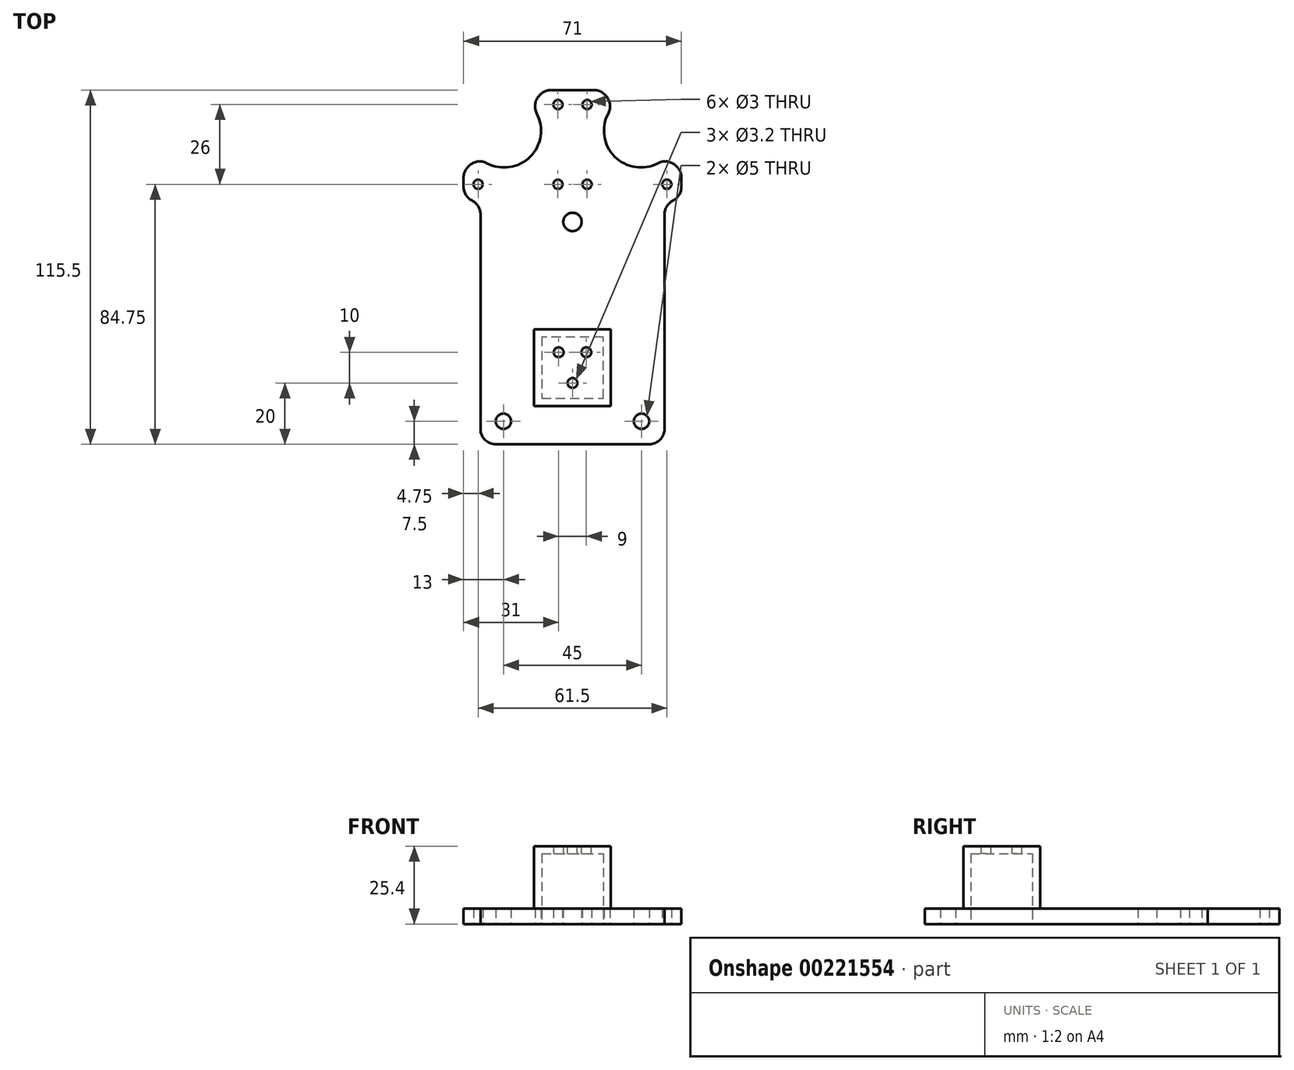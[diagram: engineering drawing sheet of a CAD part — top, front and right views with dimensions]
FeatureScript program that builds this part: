
annotation { "Feature Type Name" : "Feature", "Feature Type Description" : "" }
export const myFeature = defineFeature(function(context is Context, id is Id, definition is map)
    precondition{}
    {
        {
            var Q0;
            Q0=qCreatedBy(makeId("Top.planeOp"),FACE);
            var sketch = newSketch(context, id + "F0", { "sketchPlane" : qUnion([Q0])});
            skLineSegment(sketch, "E0.bottom", {"start": v(0, 0) * mm, "end": v(60, 0) * mm});
            skLineSegment(sketch, "E0.left", {"start": v(0, 0) * mm, "end": v(0, 80) * mm});
            skLineSegment(sketch, "E0.right", {"start": v(60, 0) * mm, "end": v(60, 80) * mm});
            skCircle(sketch, "E1", {"center": v(30, 72.5) * mm, "radius": 3 * mm});
            skCircle(sketch, "E2", {"center": v(52.5, 7.5) * mm, "radius": 2.5 * mm});
            skCircle(sketch, "E3", {"center": v(7.5, 7.5) * mm, "radius": 2.5 * mm});
            skLineSegment(sketch, "E4", {"start": v(0, 80) * mm, "end": v(-5.5, 80) * mm});
            skLineSegment(sketch, "E5", {"start": v(60, 80) * mm, "end": v(65.5, 80) * mm});
            skLineSegment(sketch, "E6.top", {"start": v(30, 80) * mm, "end": v(-5.5, 80) * mm, "construction": true});
            skLineSegment(sketch, "E6.left", {"start": v(30, 115.5) * mm, "end": v(30, 80) * mm, "construction": true});
            skCircle(sketch, "E7", {"center": v(25.25, 110.75) * mm, "radius": 1.5 * mm});
            skCircle(sketch, "E8", {"center": v(25.25, 84.75) * mm, "radius": 1.5 * mm});
            skCircle(sketch, "E9", {"center": v(-0.75, 84.75) * mm, "radius": 1.5 * mm});
            skCircle(sketch, "E10.MirrorC", {"center": v(60.75, 84.75) * mm, "radius": 1.5 * mm});
            skCircle(sketch, "E11.MirrorC", {"center": v(34.75, 84.75) * mm, "radius": 1.5 * mm});
            skCircle(sketch, "E12.MirrorC", {"center": v(34.75, 110.75) * mm, "radius": 1.5 * mm});
            skLineSegment(sketch, "E13", {"start": v(-5.5, 80) * mm, "end": v(-5.5, 89) * mm});
            skLineSegment(sketch, "E14", {"start": v(21, 115.5) * mm, "end": v(39, 115.5) * mm});
            skArc(sketch, "E15", {"start": v(-0.74, 93.76) * mm, "mid": v(16.24, 93.76) * mm, "end": v(16.24, 110.74) * mm});
            skLineSegment(sketch, "E16", {"start": v(-5.5, 89) * mm, "end": v(-0.74, 93.76) * mm});
            skLineSegment(sketch, "E17", {"start": v(16.24, 110.74) * mm, "end": v(21, 115.5) * mm});
            skLineSegment(sketch, "E18.MirrorCS", {"start": v(65.5, 80) * mm, "end": v(65.5, 89) * mm});
            skLineSegment(sketch, "E19.MirrorCS", {"start": v(43.76, 110.74) * mm, "end": v(39, 115.5) * mm});
            skLineSegment(sketch, "E20.MirrorCS", {"start": v(65.5, 89) * mm, "end": v(60.74, 93.76) * mm});
            skArc(sketch, "E21.MirrorCS", {"start": v(60.74, 93.76) * mm, "mid": v(43.76, 93.76) * mm, "end": v(43.76, 110.74) * mm});
            skSolve(sketch);
        }
        {
            var Q0;
            Q0 = qSketchRegion(id + "F0", true);
            extrude(context, id + "F1", {"entities" : qUnion([Q0]), "depth" : 5 * mm});
        }
        {
            var Q0;
            Q0=makeQuery(id+"F1.opExtrude","SWEPT_EDGE",EDGE,{"disambiguationData":[OSD([sQuery(id+"F0.wireOp",EDGE,"E0.top"),sQuery(id+"F0.wireOp",EDGE,"E0.left")])]});
            var Q1;
            Q1=makeQuery(id+"F1.opExtrude","SWEPT_EDGE",EDGE,{"disambiguationData":[OSD([sQuery(id+"F0.wireOp",EDGE,"E0.top"),sQuery(id+"F0.wireOp",EDGE,"E0.right")])]});
            var Q2;
            Q2=makeQuery(id+"F1.opExtrude","SWEPT_EDGE",EDGE,{"disambiguationData":[OSD([sQuery(id+"F0.wireOp",EDGE,"E0.bottom"),sQuery(id+"F0.wireOp",EDGE,"E0.right")])]});
            var Q3;
            Q3=makeQuery(id+"F1.opExtrude","SWEPT_EDGE",EDGE,{"disambiguationData":[OSD([sQuery(id+"F0.wireOp",EDGE,"E0.bottom"),sQuery(id+"F0.wireOp",EDGE,"E0.left")])]});
            fillet(context, id + "F2", {"entities" : qUnion([Q0, Q1, Q2, Q3]), "radius" : 5 * mm, "tangentPropagation" : true, "allowEdgeOverflow" : false});
        }
        {
            var Q0;
            Q0=makeQuery(id+"F1.opExtrude","SWEPT_EDGE",EDGE,{"disambiguationData":[OSD([sQuery(id+"F0.wireOp",EDGE,"E4"),sQuery(id+"F0.wireOp",EDGE,"E13")])]});
            var Q1;
            Q1=makeQuery(id+"F1.opExtrude","SWEPT_EDGE",EDGE,{"disambiguationData":[OSD([sQuery(id+"F0.wireOp",EDGE,"E13"),sQuery(id+"F0.wireOp",EDGE,"E16")])]});
            var Q2;
            Q2=makeQuery(id+"F1.opExtrude","SWEPT_EDGE",EDGE,{"disambiguationData":[OSD([sQuery(id+"F0.wireOp",EDGE,"E15"),sQuery(id+"F0.wireOp",EDGE,"E16")])]});
            var Q3;
            Q3=makeQuery(id+"F1.opExtrude","SWEPT_EDGE",EDGE,{"disambiguationData":[OSD([sQuery(id+"F0.wireOp",EDGE,"E15"),sQuery(id+"F0.wireOp",EDGE,"E17")])]});
            var Q4;
            Q4=makeQuery(id+"F1.opExtrude","SWEPT_EDGE",EDGE,{"disambiguationData":[OSD([sQuery(id+"F0.wireOp",EDGE,"E14"),sQuery(id+"F0.wireOp",EDGE,"E17")])]});
            var Q5;
            Q5=makeQuery(id+"F1.opExtrude","SWEPT_EDGE",EDGE,{"disambiguationData":[OSD([sQuery(id+"F0.wireOp",EDGE,"E5"),sQuery(id+"F0.wireOp",EDGE,"E18.MirrorCS")])]});
            var Q6;
            Q6=makeQuery(id+"F1.opExtrude","SWEPT_EDGE",EDGE,{"disambiguationData":[OSD([sQuery(id+"F0.wireOp",EDGE,"E18.MirrorCS"),sQuery(id+"F0.wireOp",EDGE,"E20.MirrorCS")])]});
            var Q7;
            Q7=makeQuery(id+"F1.opExtrude","SWEPT_EDGE",EDGE,{"disambiguationData":[OSD([sQuery(id+"F0.wireOp",EDGE,"E20.MirrorCS"),sQuery(id+"F0.wireOp",EDGE,"E21.MirrorCS")])]});
            var Q8;
            Q8=makeQuery(id+"F1.opExtrude","SWEPT_EDGE",EDGE,{"disambiguationData":[OSD([sQuery(id+"F0.wireOp",EDGE,"E19.MirrorCS"),sQuery(id+"F0.wireOp",EDGE,"E21.MirrorCS")])]});
            var Q9;
            Q9=makeQuery(id+"F1.opExtrude","SWEPT_EDGE",EDGE,{"disambiguationData":[OSD([sQuery(id+"F0.wireOp",EDGE,"E14"),sQuery(id+"F0.wireOp",EDGE,"E19.MirrorCS")])]});
            fillet(context, id + "F3", {"entities" : qUnion([Q0, Q1, Q2, Q3, Q4, Q5, Q6, Q7, Q8, Q9]), "radius" : 5 * mm, "tangentPropagation" : true, "allowEdgeOverflow" : false});
        }
        {
            var Q0;
            Q0=makeQuery(id+"F1.opExtrude","CAP_FACE",FACE,{"disambiguationData":[OSD([sQuery(id+"F0.wireOp",EDGE,"E0.bottom"),sQuery(id+"F0.wireOp",EDGE,"E0.left"),sQuery(id+"F0.wireOp",EDGE,"E0.right"),sQuery(id+"F0.wireOp",EDGE,"E1"),sQuery(id+"F0.wireOp",EDGE,"E2"),sQuery(id+"F0.wireOp",EDGE,"E3"),sQuery(id+"F0.wireOp",EDGE,"E4"),sQuery(id+"F0.wireOp",EDGE,"E5"),sQuery(id+"F0.wireOp",EDGE,"E7"),sQuery(id+"F0.wireOp",EDGE,"E8"),sQuery(id+"F0.wireOp",EDGE,"E9"),sQuery(id+"F0.wireOp",EDGE,"E10.MirrorC"),sQuery(id+"F0.wireOp",EDGE,"E11.MirrorC"),sQuery(id+"F0.wireOp",EDGE,"E12.MirrorC"),sQuery(id+"F0.wireOp",EDGE,"E13"),sQuery(id+"F0.wireOp",EDGE,"E14"),sQuery(id+"F0.wireOp",EDGE,"E15"),sQuery(id+"F0.wireOp",EDGE,"E16"),sQuery(id+"F0.wireOp",EDGE,"E17"),sQuery(id+"F0.wireOp",EDGE,"E18.MirrorCS"),sQuery(id+"F0.wireOp",EDGE,"E19.MirrorCS"),sQuery(id+"F0.wireOp",EDGE,"E20.MirrorCS"),sQuery(id+"F0.wireOp",EDGE,"E21.MirrorCS")])],"isStart":false});
            var sketch = newSketch(context, id + "F4", { "sketchPlane" : qUnion([Q0])});
            skLineSegment(sketch, "E22.bottom", {"start": v(15, 0) * mm, "end": v(45, 0) * mm, "construction": true});
            skLineSegment(sketch, "E23", {"start": v(30, 40) * mm, "end": v(30, 10) * mm, "construction": true});
            skLineSegment(sketch, "E24.bottom", {"start": v(17.5, 37.5) * mm, "end": v(42.5, 37.5) * mm});
            skLineSegment(sketch, "E24.top", {"start": v(17.5, 12.5) * mm, "end": v(42.5, 12.5) * mm});
            skLineSegment(sketch, "E24.left", {"start": v(17.5, 37.5) * mm, "end": v(17.5, 12.5) * mm});
            skLineSegment(sketch, "E24.right", {"start": v(42.5, 37.5) * mm, "end": v(42.5, 12.5) * mm});
            skSolve(sketch);
        }
        {
            var Q0;
            Q0 = qSketchRegion(id + "F4", true);
            extrude(context, id + "F5", {"entities" : qUnion([Q0]), "operationType" : NewBodyOperationType.ADD, "depth" : 20.4 * mm});
        }
        {
            var Q0;
            Q0=makeQuery(id+"F1.opExtrude","CAP_FACE",FACE,{"disambiguationData":[OSD([sQuery(id+"F0.wireOp",EDGE,"E0.bottom"),sQuery(id+"F0.wireOp",EDGE,"E0.left"),sQuery(id+"F0.wireOp",EDGE,"E0.right"),sQuery(id+"F0.wireOp",EDGE,"E1"),sQuery(id+"F0.wireOp",EDGE,"E2"),sQuery(id+"F0.wireOp",EDGE,"E3"),sQuery(id+"F0.wireOp",EDGE,"E4"),sQuery(id+"F0.wireOp",EDGE,"E5"),sQuery(id+"F0.wireOp",EDGE,"E7"),sQuery(id+"F0.wireOp",EDGE,"E8"),sQuery(id+"F0.wireOp",EDGE,"E9"),sQuery(id+"F0.wireOp",EDGE,"E10.MirrorC"),sQuery(id+"F0.wireOp",EDGE,"E11.MirrorC"),sQuery(id+"F0.wireOp",EDGE,"E12.MirrorC"),sQuery(id+"F0.wireOp",EDGE,"E13"),sQuery(id+"F0.wireOp",EDGE,"E14"),sQuery(id+"F0.wireOp",EDGE,"E15"),sQuery(id+"F0.wireOp",EDGE,"E16"),sQuery(id+"F0.wireOp",EDGE,"E17"),sQuery(id+"F0.wireOp",EDGE,"E18.MirrorCS"),sQuery(id+"F0.wireOp",EDGE,"E19.MirrorCS"),sQuery(id+"F0.wireOp",EDGE,"E20.MirrorCS"),sQuery(id+"F0.wireOp",EDGE,"E21.MirrorCS")])],"isStart":true});
            var sketch = newSketch(context, id + "F6", { "sketchPlane" : qUnion([Q0])});
            skLineSegment(sketch, "E25.0.0", {"start": v(17.5, -37.5) * mm, "end": v(17.5, -12.5) * mm, "construction": true});
            skLineSegment(sketch, "E25.0.1", {"start": v(17.5, -12.5) * mm, "end": v(42.5, -12.5) * mm, "construction": true});
            skLineSegment(sketch, "E25.0.2", {"start": v(42.5, -12.5) * mm, "end": v(42.5, -37.5) * mm, "construction": true});
            skLineSegment(sketch, "E25.0.3", {"start": v(42.5, -37.5) * mm, "end": v(17.5, -37.5) * mm, "construction": true});
            skLineSegment(sketch, "E26.0", {"start": v(40, -15) * mm, "end": v(40, -35) * mm});
            skLineSegment(sketch, "E26.1", {"start": v(20, -15) * mm, "end": v(40, -15) * mm});
            skLineSegment(sketch, "E26.2", {"start": v(20, -35) * mm, "end": v(20, -15) * mm});
            skLineSegment(sketch, "E26.3", {"start": v(40, -35) * mm, "end": v(20, -35) * mm});
            skSolve(sketch);
        }
        {
            var Q0;
            Q0 = qSketchRegion(id + "F6", true);
            extrude(context, id + "F7", {"entities" : qUnion([Q0]), "operationType" : NewBodyOperationType.REMOVE, "oppositeDirection" : true, "depth" : (25.4 - 2.5) * mm});
        }
        {
            var Q0;
            Q0=makeQuery(id+"F5.opExtrude","CAP_FACE",FACE,{"disambiguationData":[OSD([sQuery(id+"F4.wireOp",EDGE,"E24.bottom"),sQuery(id+"F4.wireOp",EDGE,"E24.top"),sQuery(id+"F4.wireOp",EDGE,"E24.left"),sQuery(id+"F4.wireOp",EDGE,"E24.right")])],"isStart":false});
            var sketch = newSketch(context, id + "F8", { "sketchPlane" : qUnion([Q0])});
            skLineSegment(sketch, "E27", {"start": v(30, 37.5) * mm, "end": v(30, 12.5) * mm, "construction": true});
            skCircle(sketch, "E28", {"center": v(25.5, 30) * mm, "radius": 1.6 * mm});
            skCircle(sketch, "E29", {"center": v(30, 20) * mm, "radius": 1.6 * mm});
            skCircle(sketch, "E30.MirrorC", {"center": v(34.5, 30) * mm, "radius": 1.6 * mm});
            skSolve(sketch);
        }
        {
            var Q0;
            Q0 = qSketchRegion(id + "F8", true);
            extrude(context, id + "F9", {"entities" : qUnion([Q0]), "operationType" : NewBodyOperationType.REMOVE, "endBound" : BoundingType.THROUGH_ALL, "oppositeDirection" : true, "depth" : 25 * mm});
        }
    });
